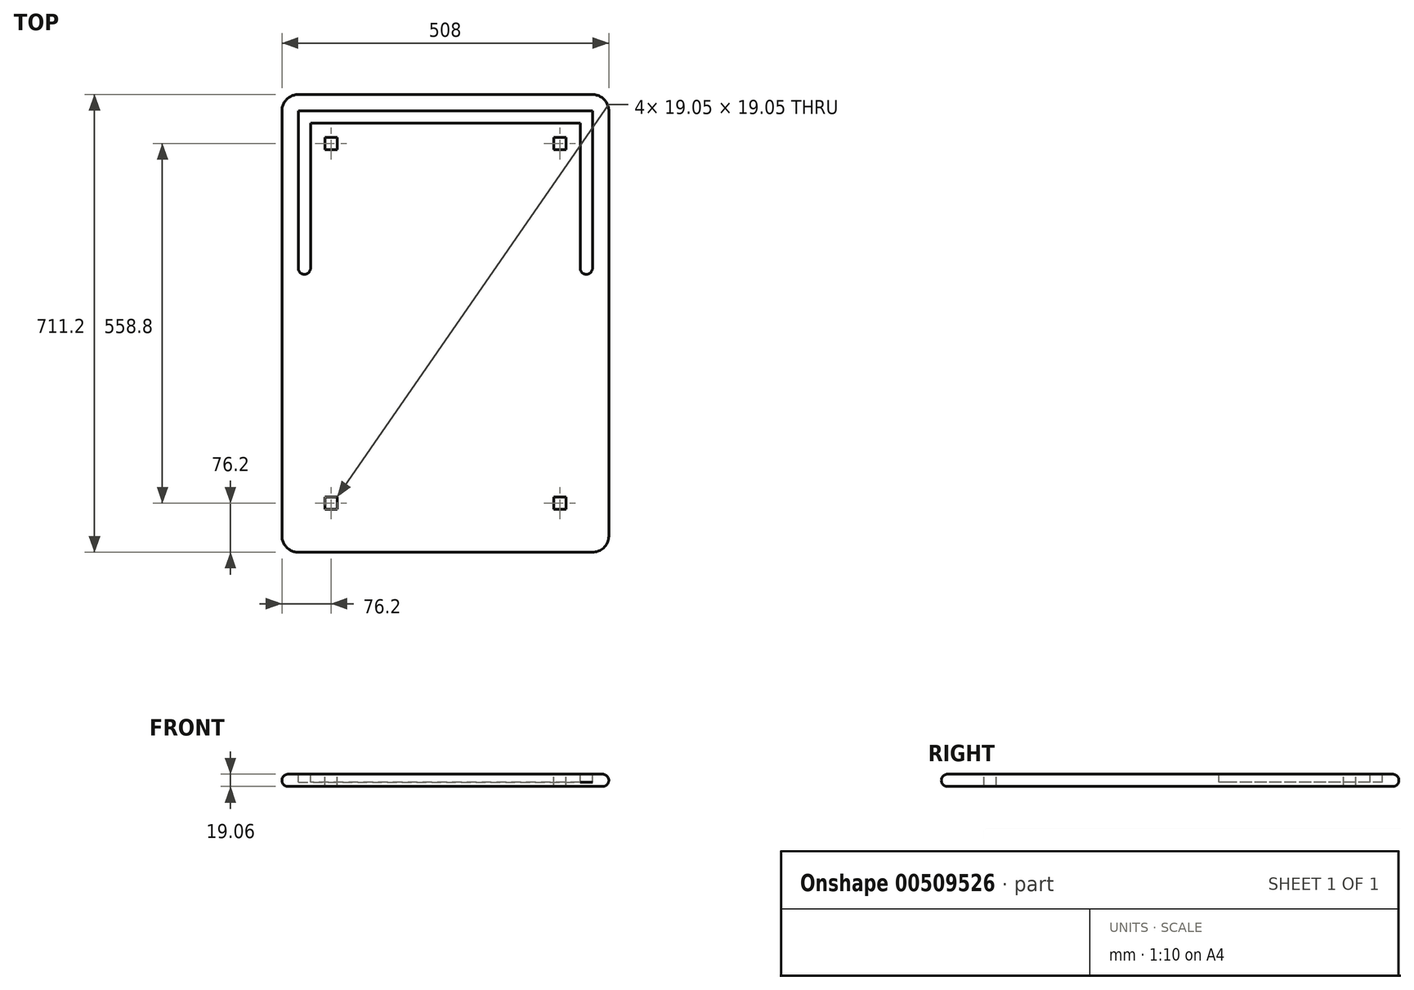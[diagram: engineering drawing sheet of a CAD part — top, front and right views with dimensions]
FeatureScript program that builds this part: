
annotation { "Feature Type Name" : "Feature", "Feature Type Description" : "" }
export const myFeature = defineFeature(function(context is Context, id is Id, definition is map)
    precondition{}
    {
        {
            var Q0;
            Q0=qCreatedBy(makeId("Top.planeOp"),FACE);
            var sketch = newSketch(context, id + "F0", { "sketchPlane" : qUnion([Q0])});
            skLineSegment(sketch, "E0.bottom", {"start": v(-228.6, 355.6) * mm, "end": v(228.6, 355.6) * mm});
            skLineSegment(sketch, "E0.top", {"start": v(-228.6, -355.6) * mm, "end": v(228.6, -355.6) * mm});
            skLineSegment(sketch, "E0.left", {"start": v(-254, 330.2) * mm, "end": v(-254, -330.2) * mm});
            skLineSegment(sketch, "E0.right", {"start": v(254, 330.2) * mm, "end": v(254, -330.2) * mm});
            skPoint(sketch, "E0.middle", {"position": v(0, 0) * mm});
            skPoint(sketch, "E1.visualSharp", {"position": v(-254, 355.6) * mm});
            skPoint(sketch, "E2.visualSharp", {"position": v(254, 355.6) * mm});
            skPoint(sketch, "E3.visualSharp", {"position": v(254, -355.6) * mm});
            skArc(sketch, "E3.filletArc", {"start": v(228.6, -355.6) * mm, "mid": v(246.56, -348.16) * mm, "end": v(254, -330.2) * mm});
            skPoint(sketch, "E4.visualSharp", {"position": v(-254, -355.6) * mm});
            skArc(sketch, "E4.filletArc", {"start": v(-254, -330.2) * mm, "mid": v(-246.56, -348.16) * mm, "end": v(-228.6, -355.6) * mm});
            skArc(sketch, "E5.filletArc", {"start": v(-228.6, 355.6) * mm, "mid": v(-246.56, 348.16) * mm, "end": v(-254, 330.2) * mm});
            skArc(sketch, "E6.filletArc", {"start": v(254, 330.2) * mm, "mid": v(246.56, 348.16) * mm, "end": v(228.6, 355.6) * mm});
            skSolve(sketch);
        }
        {
            var Q0;
            Q0=makeQuery(id+"F0.imprint","IMPRINT",FACE,{"disambiguationData":[TD([[makeQuery(id+"F0.imprint","IMPRINT",EDGE,{"derivedFrom":sQuery(id+"F0.wireOp",EDGE,"E0.bottom")}),-1.0]])]});
            extrude(context, id + "F1", {"entities" : qUnion([Q0]), "endBound" : BoundingType.SYMMETRIC, "depth" : 19.05 * mm, "offsetDistance" : 25.4 * mm});
        }
        {
            var Q0;
            Q0=makeQuery(id+"F1.opExtrude","CAP_FACE",FACE,{"disambiguationData":[OSD([sQuery(id+"F0.wireOp",EDGE,"E0.bottom"),sQuery(id+"F0.wireOp",EDGE,"E0.top"),sQuery(id+"F0.wireOp",EDGE,"E0.left"),sQuery(id+"F0.wireOp",EDGE,"E0.right"),sQuery(id+"F0.wireOp",EDGE,"E3.filletArc"),sQuery(id+"F0.wireOp",EDGE,"E4.filletArc"),sQuery(id+"F0.wireOp",EDGE,"E5.filletArc"),sQuery(id+"F0.wireOp",EDGE,"E6.filletArc")])],"isStart":false});
            var Q1;
            Q1=makeQuery(id+"F1.opExtrude","CAP_FACE",FACE,{"disambiguationData":[OSD([sQuery(id+"F0.wireOp",EDGE,"E0.bottom"),sQuery(id+"F0.wireOp",EDGE,"E0.top"),sQuery(id+"F0.wireOp",EDGE,"E0.left"),sQuery(id+"F0.wireOp",EDGE,"E0.right"),sQuery(id+"F0.wireOp",EDGE,"E3.filletArc"),sQuery(id+"F0.wireOp",EDGE,"E4.filletArc"),sQuery(id+"F0.wireOp",EDGE,"E5.filletArc"),sQuery(id+"F0.wireOp",EDGE,"E6.filletArc")])],"isStart":true});
            fillet(context, id + "F2", {"entities" : qUnion([Q0, Q1]), "radius" : 9.52 * mm, "tangentPropagation" : true, "allowEdgeOverflow" : false});
        }
        {
            var Q0;
            Q0=makeQuery(id+"F1.opExtrude","CAP_FACE",FACE,{"disambiguationData":[OSD([sQuery(id+"F0.wireOp",EDGE,"E0.bottom"),sQuery(id+"F0.wireOp",EDGE,"E0.top"),sQuery(id+"F0.wireOp",EDGE,"E0.left"),sQuery(id+"F0.wireOp",EDGE,"E0.right"),sQuery(id+"F0.wireOp",EDGE,"E3.filletArc"),sQuery(id+"F0.wireOp",EDGE,"E4.filletArc")])],"isStart":false});
            var sketch = newSketch(context, id + "F3", { "sketchPlane" : qUnion([Q0])});
            skLineSegment(sketch, "E7", {"start": v(228.6, 330.2) * mm, "end": v(228.6, 85.73) * mm});
            skLineSegment(sketch, "E8", {"start": v(219.08, 76.2) * mm, "end": v(219.08, 76.2) * mm});
            skLineSegment(sketch, "E9", {"start": v(209.55, 85.73) * mm, "end": v(209.55, 311.15) * mm});
            skLineSegment(sketch, "E10", {"start": v(209.55, 311.15) * mm, "end": v(-209.55, 311.15) * mm});
            skLineSegment(sketch, "E11", {"start": v(-209.55, 311.15) * mm, "end": v(-209.55, 85.73) * mm});
            skLineSegment(sketch, "E12", {"start": v(-219.07, 76.2) * mm, "end": v(-219.07, 76.2) * mm});
            skLineSegment(sketch, "E13", {"start": v(-228.6, 85.73) * mm, "end": v(-228.6, 330.2) * mm});
            skLineSegment(sketch, "E14", {"start": v(-228.6, 330.2) * mm, "end": v(228.6, 330.2) * mm});
            skPoint(sketch, "E15.visualSharp", {"position": v(228.6, 76.2) * mm});
            skArc(sketch, "E15.filletArc", {"start": v(219.08, 76.2) * mm, "mid": v(225.81, 78.99) * mm, "end": v(228.6, 85.73) * mm});
            skPoint(sketch, "E16.visualSharp", {"position": v(209.55, 76.2) * mm});
            skArc(sketch, "E16.filletArc", {"start": v(209.55, 85.73) * mm, "mid": v(212.34, 78.99) * mm, "end": v(219.08, 76.2) * mm});
            skPoint(sketch, "E17.visualSharp", {"position": v(-209.55, 76.2) * mm});
            skArc(sketch, "E17.filletArc", {"start": v(-219.07, 76.2) * mm, "mid": v(-212.34, 78.99) * mm, "end": v(-209.55, 85.73) * mm});
            skPoint(sketch, "E18.visualSharp", {"position": v(-228.6, 76.2) * mm});
            skArc(sketch, "E18.filletArc", {"start": v(-228.6, 85.73) * mm, "mid": v(-225.81, 78.99) * mm, "end": v(-219.07, 76.2) * mm});
            skSolve(sketch);
        }
        {
            var Q0;
            Q0=makeQuery(id+"F3.imprint","IMPRINT",FACE,{"disambiguationData":[TD([[makeQuery(id+"F3.imprint","IMPRINT",EDGE,{"derivedFrom":sQuery(id+"F3.wireOp",EDGE,"E7")}),-1.0]])]});
            extrude(context, id + "F4", {"entities" : qUnion([Q0]), "operationType" : NewBodyOperationType.REMOVE, "oppositeDirection" : true, "depth" : 12.7 * mm, "offsetDistance" : 25.4 * mm});
        }
        {
            var Q0;
            Q0=makeQuery(id+"F1.opExtrude","CAP_FACE",FACE,{"disambiguationData":[OSD([sQuery(id+"F0.wireOp",EDGE,"E0.bottom"),sQuery(id+"F0.wireOp",EDGE,"E0.top"),sQuery(id+"F0.wireOp",EDGE,"E0.left"),sQuery(id+"F0.wireOp",EDGE,"E0.right"),sQuery(id+"F0.wireOp",EDGE,"E3.filletArc"),sQuery(id+"F0.wireOp",EDGE,"E4.filletArc"),sQuery(id+"F0.wireOp",EDGE,"E5.filletArc"),sQuery(id+"F0.wireOp",EDGE,"E6.filletArc")])],"isStart":false});
            var sketch = newSketch(context, id + "F5", { "sketchPlane" : qUnion([Q0])});
            skLineSegment(sketch, "E19.bottom", {"start": v(-187.33, 288.92) * mm, "end": v(-168.28, 288.92) * mm});
            skLineSegment(sketch, "E19.top", {"start": v(-187.33, 269.87) * mm, "end": v(-168.28, 269.87) * mm});
            skLineSegment(sketch, "E19.left", {"start": v(-187.33, 288.92) * mm, "end": v(-187.33, 269.87) * mm});
            skLineSegment(sketch, "E19.right", {"start": v(-168.28, 288.92) * mm, "end": v(-168.28, 269.87) * mm});
            skPoint(sketch, "E19.middle", {"position": v(-177.8, 279.4) * mm});
            skLineSegment(sketch, "E20.bottom", {"start": v(168.28, 288.93) * mm, "end": v(187.33, 288.93) * mm});
            skLineSegment(sketch, "E20.top", {"start": v(168.28, 269.88) * mm, "end": v(187.33, 269.88) * mm});
            skLineSegment(sketch, "E20.left", {"start": v(168.28, 288.93) * mm, "end": v(168.28, 269.88) * mm});
            skLineSegment(sketch, "E20.right", {"start": v(187.33, 288.93) * mm, "end": v(187.33, 269.88) * mm});
            skPoint(sketch, "E20.middle", {"position": v(177.8, 279.4) * mm});
            skLineSegment(sketch, "E21.bottom", {"start": v(-187.33, -269.88) * mm, "end": v(-168.28, -269.88) * mm});
            skLineSegment(sketch, "E21.top", {"start": v(-187.33, -288.93) * mm, "end": v(-168.28, -288.93) * mm});
            skLineSegment(sketch, "E21.left", {"start": v(-187.33, -269.88) * mm, "end": v(-187.33, -288.93) * mm});
            skLineSegment(sketch, "E21.right", {"start": v(-168.28, -269.88) * mm, "end": v(-168.28, -288.93) * mm});
            skPoint(sketch, "E21.middle", {"position": v(-177.8, -279.4) * mm});
            skLineSegment(sketch, "E22.bottom", {"start": v(168.27, -269.88) * mm, "end": v(187.32, -269.88) * mm});
            skLineSegment(sketch, "E22.top", {"start": v(168.27, -288.93) * mm, "end": v(187.32, -288.93) * mm});
            skLineSegment(sketch, "E22.left", {"start": v(168.27, -269.88) * mm, "end": v(168.27, -288.93) * mm});
            skLineSegment(sketch, "E22.right", {"start": v(187.32, -269.88) * mm, "end": v(187.32, -288.93) * mm});
            skPoint(sketch, "E22.middle", {"position": v(177.8, -279.4) * mm});
            skLineSegment(sketch, "E23", {"start": v(0, 0) * mm, "end": v(-254, 0) * mm});
            skLineSegment(sketch, "E24", {"start": v(0, 0) * mm, "end": v(254, 0) * mm});
            skSolve(sketch);
        }
        {
            var Q0;
            Q0=makeQuery(id+"F5.imprint","IMPRINT",FACE,{"disambiguationData":[TD([[makeQuery(id+"F5.imprint","IMPRINT",EDGE,{"derivedFrom":sQuery(id+"F5.wireOp",EDGE,"E19.bottom")}),-1.0]])]});
            var Q1;
            Q1=makeQuery(id+"F5.imprint","IMPRINT",FACE,{"disambiguationData":[TD([[makeQuery(id+"F5.imprint","IMPRINT",EDGE,{"derivedFrom":sQuery(id+"F5.wireOp",EDGE,"E20.bottom")}),-1.0]])]});
            var Q2;
            Q2=makeQuery(id+"F5.imprint","IMPRINT",FACE,{"disambiguationData":[TD([[makeQuery(id+"F5.imprint","IMPRINT",EDGE,{"derivedFrom":sQuery(id+"F5.wireOp",EDGE,"E21.bottom")}),-1.0]])]});
            var Q3;
            Q3=makeQuery(id+"F5.imprint","IMPRINT",FACE,{"disambiguationData":[TD([[makeQuery(id+"F5.imprint","IMPRINT",EDGE,{"derivedFrom":sQuery(id+"F5.wireOp",EDGE,"E22.bottom")}),-1.0]])]});
            extrude(context, id + "F6", {"entities" : qUnion([Q0, Q1, Q2, Q3]), "operationType" : NewBodyOperationType.REMOVE, "endBound" : BoundingType.THROUGH_ALL, "oppositeDirection" : true, "depth" : 25.4 * mm});
        }
    });
